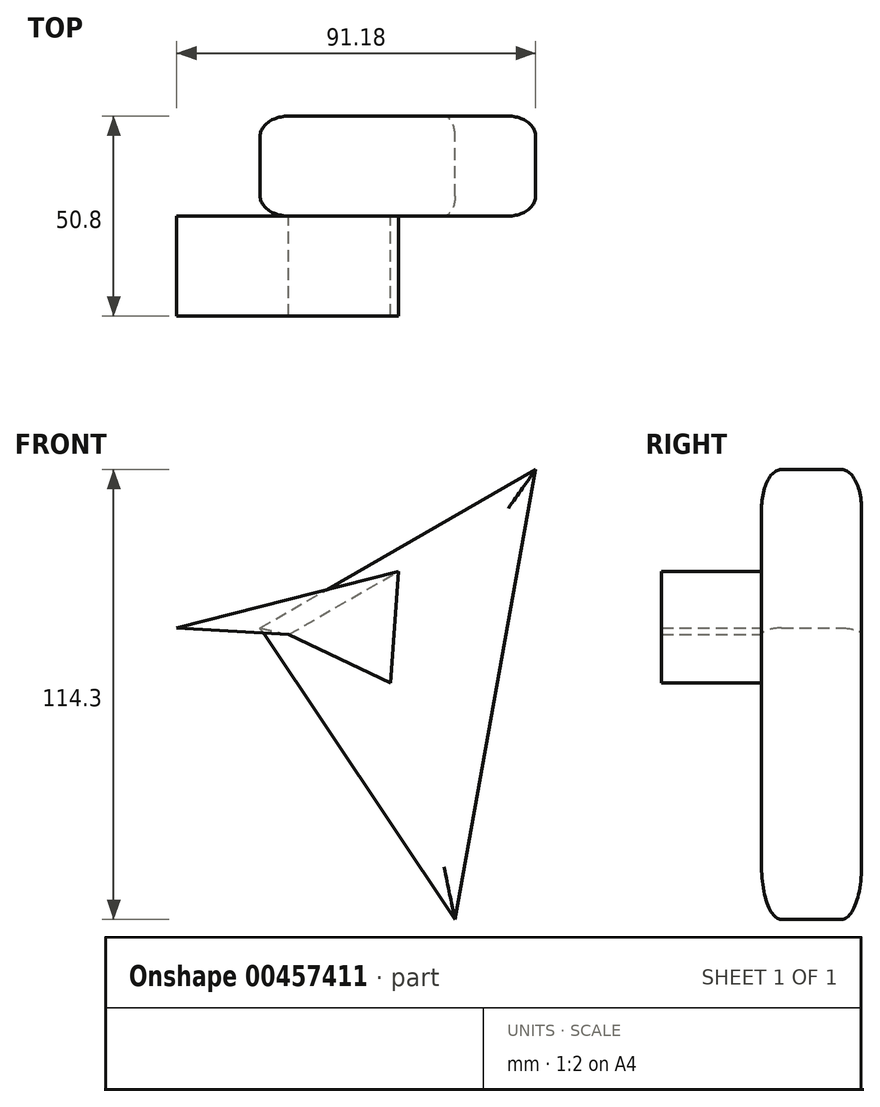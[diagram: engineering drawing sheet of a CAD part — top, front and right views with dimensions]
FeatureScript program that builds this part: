
annotation { "Feature Type Name" : "Feature", "Feature Type Description" : "" }
export const myFeature = defineFeature(function(context is Context, id is Id, definition is map)
    precondition{}
    {
        {
            var Q0;
            Q0=qCreatedBy(makeId("Front.planeOp"),FACE);
            var sketch = newSketch(context, id + "F0", { "sketchPlane" : qUnion([Q0])});
            skLineSegment(sketch, "E0", {"start": v(0, 0) * mm, "end": v(69.98, 40.26) * mm});
            skLineSegment(sketch, "E1", {"start": v(69.98, 40.26) * mm, "end": v(49.5, -74.04) * mm});
            skLineSegment(sketch, "E2", {"start": v(49.5, -74.04) * mm, "end": v(0, 0) * mm});
            skSolve(sketch);
        }
        {
            var Q0;
            Q0 = qSketchRegion(id + "F0", true);
            extrude(context, id + "F1", {"entities" : qUnion([Q0]), "depth" : 25.4 * mm});
        }
        {
            var Q0;
            Q0=makeQuery(id+"F1.opExtrude","CAP_FACE",FACE,{"disambiguationData":[OSD([sQuery(id+"F0.wireOp",EDGE,"E0"),sQuery(id+"F0.wireOp",EDGE,"E1"),sQuery(id+"F0.wireOp",EDGE,"E2")])],"isStart":false});
            fillet(context, id + "F2", {"entities" : qUnion([Q0]), "radius" : 5.08 * mm, "tangentPropagation" : true, "allowEdgeOverflow" : false});
        }
        {
            var Q0;
            Q0=makeQuery(id+"F1.opExtrude","CAP_FACE",FACE,{"disambiguationData":[OSD([sQuery(id+"F0.wireOp",EDGE,"E0"),sQuery(id+"F0.wireOp",EDGE,"E1"),sQuery(id+"F0.wireOp",EDGE,"E2")])],"isStart":true});
            fillet(context, id + "F3", {"entities" : qUnion([Q0]), "radius" : 5.08 * mm, "tangentPropagation" : true, "allowEdgeOverflow" : false});
        }
        {
            var Q0;
            Q0=makeQuery(id+"F1.opExtrude","CAP_FACE",FACE,{"disambiguationData":[OSD([sQuery(id+"F0.wireOp",EDGE,"E0"),sQuery(id+"F0.wireOp",EDGE,"E1"),sQuery(id+"F0.wireOp",EDGE,"E2")])],"isStart":false});
            var sketch = newSketch(context, id + "F4", { "sketchPlane" : qUnion([Q0])});
            skLineSegment(sketch, "E3", {"start": v(7.24, -1.7) * mm, "end": v(33.17, -14) * mm});
            skLineSegment(sketch, "E4", {"start": v(33.17, -14) * mm, "end": v(35.15, 14.36) * mm});
            skLineSegment(sketch, "E5", {"start": v(35.15, 14.36) * mm, "end": v(-21.2, 0) * mm});
            skLineSegment(sketch, "E6", {"start": v(-21.2, 0) * mm, "end": v(7.24, -1.7) * mm});
            skSolve(sketch);
        }
        {
            var Q0;
            Q0 = qSketchRegion(id + "F4", true);
            extrude(context, id + "F5", {"entities" : qUnion([Q0]), "operationType" : NewBodyOperationType.ADD, "depth" : 25.4 * mm});
        }
    });
